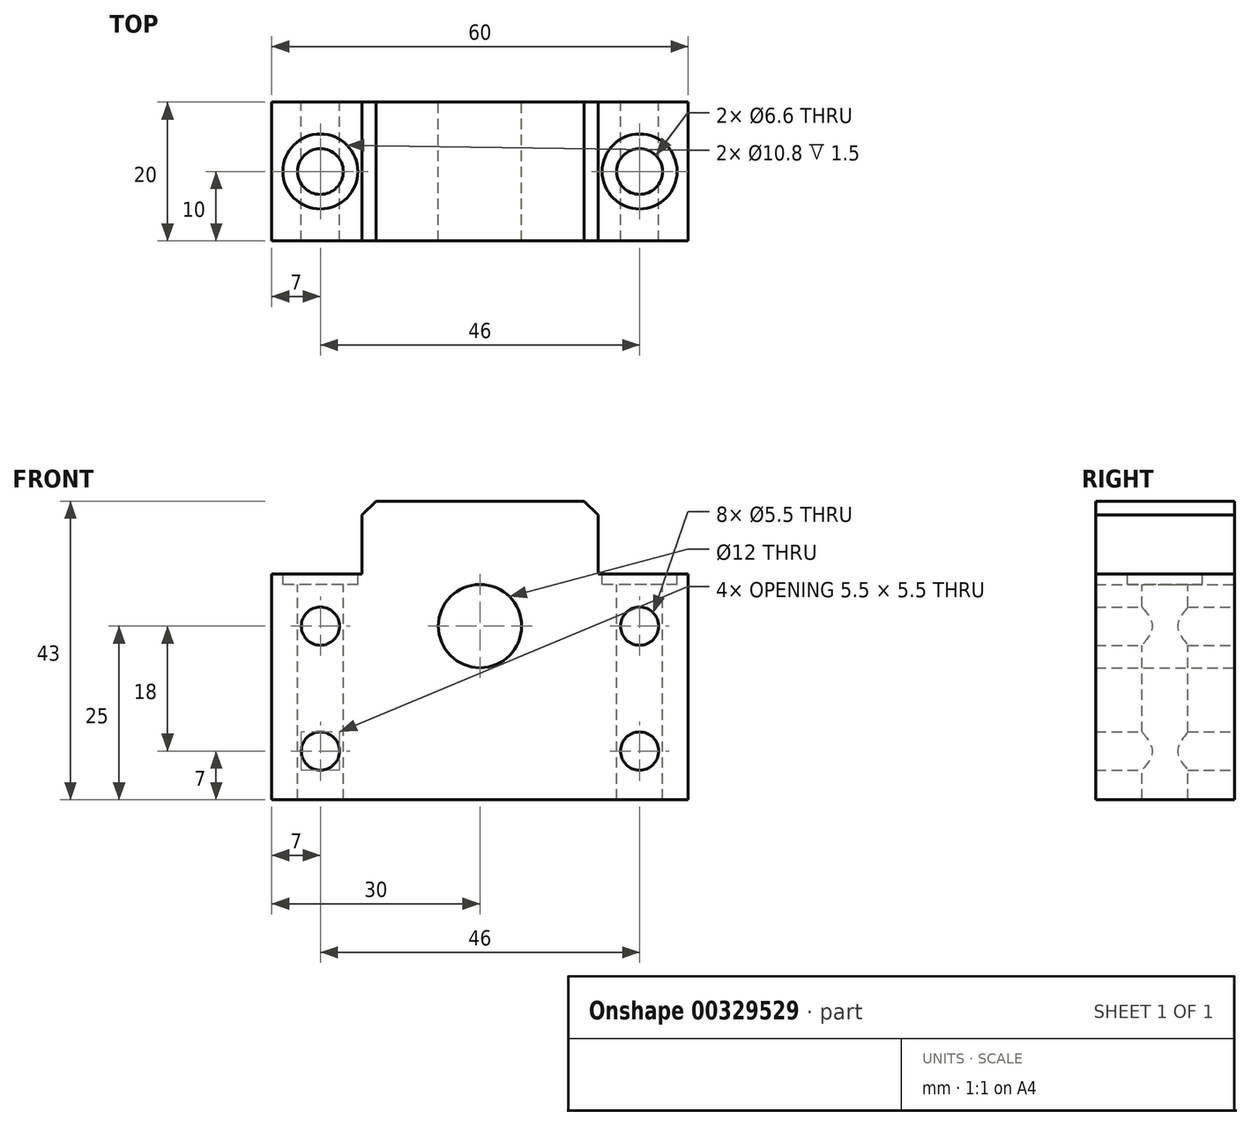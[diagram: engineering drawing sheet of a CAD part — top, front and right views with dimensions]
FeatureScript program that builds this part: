
annotation { "Feature Type Name" : "Feature", "Feature Type Description" : "" }
export const myFeature = defineFeature(function(context is Context, id is Id, definition is map)
    precondition{}
    {
        {
            var Q0;
            Q0=qCreatedBy(makeId("Front.planeOp"),FACE);
            var sketch = newSketch(context, id + "F0", { "sketchPlane" : qUnion([Q0])});
            skCircle(sketch, "E0", {"center": v(0, 0) * mm, "radius": 6 * mm});
            skLineSegment(sketch, "E1.bottom", {"start": v(-30, -25) * mm, "end": v(30, -25) * mm});
            skLineSegment(sketch, "E1.top", {"start": v(-30, 7.5) * mm, "end": v(-17, 7.5) * mm});
            skLineSegment(sketch, "E1.left", {"start": v(-30, -25) * mm, "end": v(-30, 7.5) * mm});
            skLineSegment(sketch, "E1.right", {"start": v(30, -25) * mm, "end": v(30, 7.5) * mm});
            skLineSegment(sketch, "E2.top", {"start": v(-15, 18) * mm, "end": v(15, 18) * mm});
            skLineSegment(sketch, "E2.left", {"start": v(-17, 7.5) * mm, "end": v(-17, 16) * mm});
            skLineSegment(sketch, "E2.right", {"start": v(17, 7.5) * mm, "end": v(17, 16) * mm});
            skLineSegment(sketch, "E3.trimOffspring", {"start": v(17, 7.5) * mm, "end": v(30, 7.5) * mm});
            skCircle(sketch, "E4", {"center": v(-23, 0) * mm, "radius": 2.75 * mm});
            skCircle(sketch, "E5", {"center": v(-23, -18) * mm, "radius": 2.75 * mm});
            skCircle(sketch, "E6", {"center": v(23, -18) * mm, "radius": 2.75 * mm});
            skCircle(sketch, "E7", {"center": v(23, 0) * mm, "radius": 2.75 * mm});
            skLineSegment(sketch, "E8", {"start": v(-15, 18) * mm, "end": v(-17, 16) * mm});
            skLineSegment(sketch, "E9", {"start": v(15, 18) * mm, "end": v(17, 16) * mm});
            skPoint(sketch, "E10.orphan", {"position": v(-17, 18) * mm});
            skPoint(sketch, "E11.orphan", {"position": v(17, 18) * mm});
            skSolve(sketch);
        }
        {
            var Q0;
            Q0=qSketchRegion(id+"F0",true);
            extrude(context, id + "F1", {"entities" : qUnion([Q0]), "endBound" : BoundingType.SYMMETRIC, "depth" : 20 * mm});
        }
        {
            var Q0;
            Q0=makeQuery(id+"F1.opExtrude","SWEPT_FACE",FACE,{"disambiguationData":[OSD([sQuery(id+"F0.wireOp",EDGE,"E3.trimOffspring")])]});
            var sketch = newSketch(context, id + "F2", { "sketchPlane" : qUnion([Q0])});
            skPoint(sketch, "E12", {"position": v(-23, 0) * mm});
            skPoint(sketch, "E13", {"position": v(23, 0) * mm});
            skSolve(sketch);
        }
        {
            var Q0;
            Q0=sQuery(id+"F2.wireOp",VERTEX,"E12");
            var Q1;
            Q1=sQuery(id+"F2.wireOp",VERTEX,"E13");
            var Q2;
            Q2=makeQuery(id+"F1.opExtrude","SWEPT_BODY",BODY,{"disambiguationData":[OSD([sQuery(id+"F0.wireOp",EDGE,"E0"),sQuery(id+"F0.wireOp",EDGE,"E1.bottom"),sQuery(id+"F0.wireOp",EDGE,"E1.top"),sQuery(id+"F0.wireOp",EDGE,"E1.left"),sQuery(id+"F0.wireOp",EDGE,"E1.right"),sQuery(id+"F0.wireOp",EDGE,"E2.top"),sQuery(id+"F0.wireOp",EDGE,"E2.left"),sQuery(id+"F0.wireOp",EDGE,"E2.right"),sQuery(id+"F0.wireOp",EDGE,"E3.trimOffspring"),sQuery(id+"F0.wireOp",EDGE,"E4"),sQuery(id+"F0.wireOp",EDGE,"E5"),sQuery(id+"F0.wireOp",EDGE,"E6"),sQuery(id+"F0.wireOp",EDGE,"E7"),sQuery(id+"F0.wireOp",EDGE,"E8"),sQuery(id+"F0.wireOp",EDGE,"E9")])]});
            hole(context, id + "F3", {"style" : HoleStyle.C_BORE, "endStyle" : HoleEndStyle.THROUGH, "holeDiameter" : 6.6 * mm, "cBoreDiameter" : 10.8 * mm, "cBoreDepth" : 1.5 * mm, "tappedDepth" : 9.6 * mm, "tapClearance" : 3, "locations" : qUnion([Q0, Q1]), "scope" : qUnion([Q2])});
        }
    });
